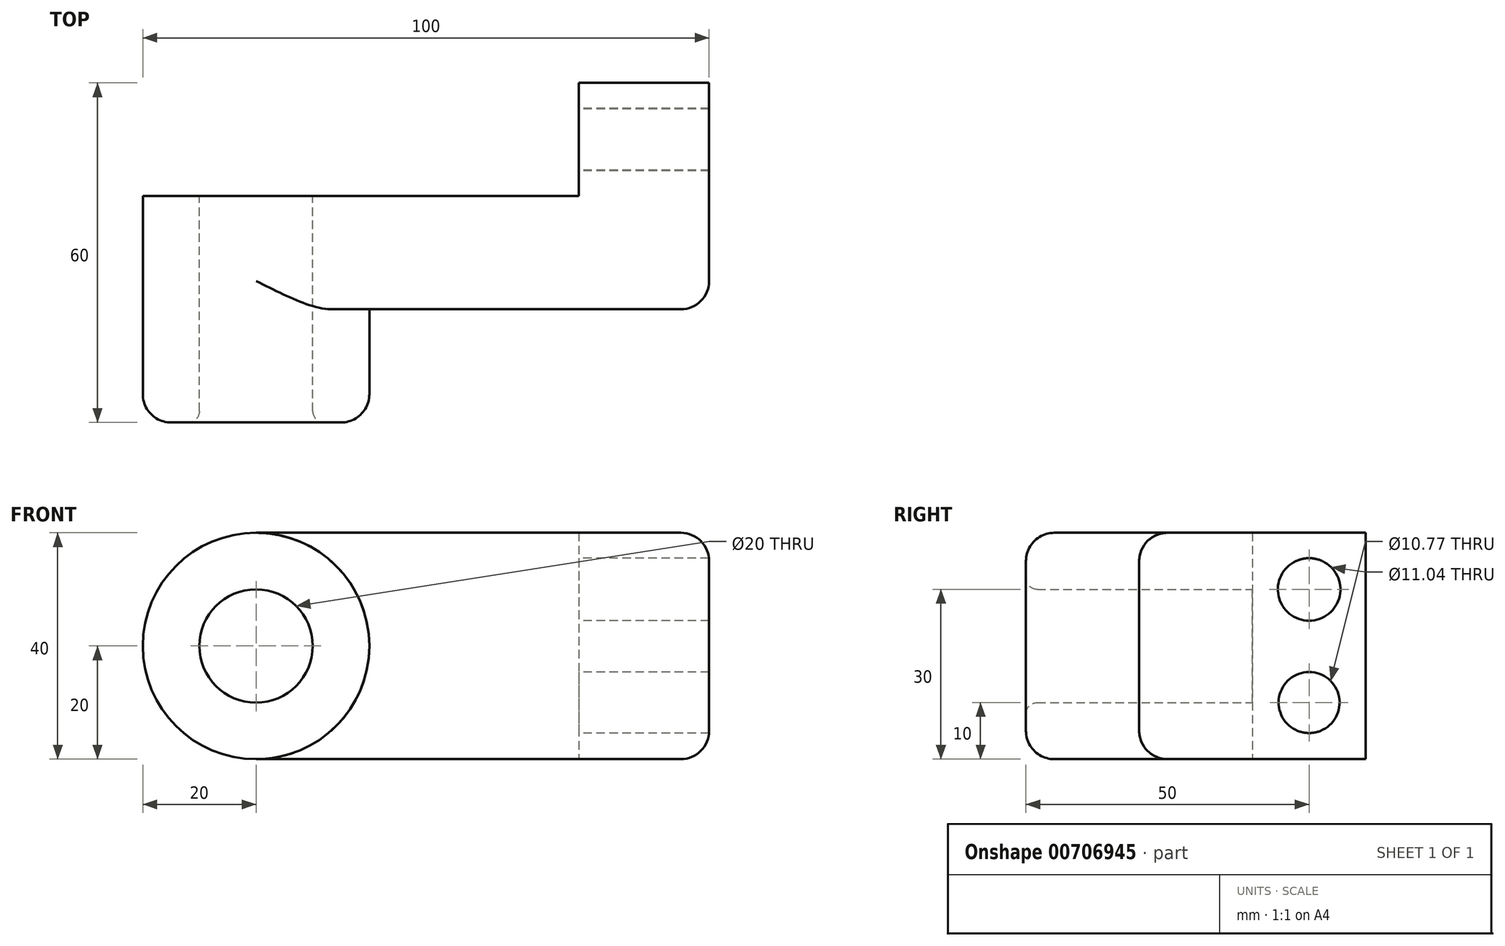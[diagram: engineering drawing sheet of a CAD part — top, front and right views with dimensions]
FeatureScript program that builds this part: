
annotation { "Feature Type Name" : "Feature", "Feature Type Description" : "" }
export const myFeature = defineFeature(function(context is Context, id is Id, definition is map)
    precondition{}
    {
        {
            var Q0;
            Q0=qCreatedBy(makeId("Front.planeOp"),FACE);
            var sketch = newSketch(context, id + "F0", { "sketchPlane" : qUnion([Q0])});
            skCircle(sketch, "E0", {"center": v(0, 0) * mm, "radius": 10 * mm});
            skCircle(sketch, "E1", {"center": v(0, 0) * mm, "radius": 20 * mm});
            skLineSegment(sketch, "E2", {"start": v(0, 20) * mm, "end": v(80, 20) * mm});
            skLineSegment(sketch, "E3", {"start": v(0, -20) * mm, "end": v(80, -20) * mm});
            skLineSegment(sketch, "E4", {"start": v(80, 20) * mm, "end": v(80, -20) * mm});
            skLineSegment(sketch, "E5", {"start": v(56.97, 20) * mm, "end": v(56.97, -20) * mm});
            skSolve(sketch);
        }
        {
            var Q0;
            Q0=makeQuery(id+"F0.imprint","IMPRINT",FACE,{"disambiguationData":[TD([[makeQuery(id+"F0.imprint","IMPRINT",EDGE,{"derivedFrom":sQuery(id+"F0.wireOp",EDGE,"E0")}),-1.0]])]});
            extrude(context, id + "F1", {"entities" : qUnion([Q0]), "surfaceOperationType" : NewSurfaceOperationType.ADD, "depth" : 40 * mm, "offsetDistance" : 25 * mm});
        }
        {
            var Q0;
            {var subQ0=sQuery(id+"F0.wireOp",EDGE,"E2");Q0=makeQuery(id+"F0.imprint","IMPRINT",FACE,{"disambiguationData":[TD([[makeQuery(id+"F0.imprint","IMPRINT",EDGE,{"derivedFrom":subQ0}),-1.0]])]});}
            extrude(context, id + "F2", {"entities" : qUnion([Q0]), "operationType" : NewBodyOperationType.ADD, "depth" : 20 * mm, "offsetDistance" : 25 * mm});
        }
        {
            var Q0;
            {var subQ0=sQuery(id+"F0.wireOp",EDGE,"E4");Q0=makeQuery(id+"F0.imprint","IMPRINT",FACE,{"disambiguationData":[TD([[makeQuery(id+"F0.imprint","IMPRINT",EDGE,{"derivedFrom":subQ0}),-1.0]])]});}
            extrude(context, id + "F3", {"entities" : qUnion([Q0]), "operationType" : NewBodyOperationType.ADD, "oppositeDirection" : true, "depth" : 20 * mm, "offsetDistance" : 25 * mm});
        }
        {
            var Q0;
            Q0=makeQuery(id+"F3.opExtrude","SWEPT_FACE",FACE,{"disambiguationData":[OSD([sQuery(id+"F0.wireOp",EDGE,"E5")])]});
            var sketch = newSketch(context, id + "F4", { "sketchPlane" : qUnion([Q0])});
            skCircle(sketch, "E6", {"center": v(-10, 10) * mm, "radius": 5.52 * mm});
            skPoint(sketch, "E6.centerSnap0", {"position": v(-10, 20) * mm});
            skCircle(sketch, "E7", {"center": v(-10, -10) * mm, "radius": 5.39 * mm});
            skPoint(sketch, "E7.centerSnap0", {"position": v(-10, -20) * mm});
            skSolve(sketch);
        }
        {
            var Q0;
            Q0 = qSketchRegion(id + "F4", true);
            extrude(context, id + "F5", {"entities" : qUnion([Q0]), "operationType" : NewBodyOperationType.REMOVE, "oppositeDirection" : true, "depth" : 28.9 * mm, "offsetDistance" : 25 * mm});
        }
        {
            var Q0;
            Q0=makeQuery(id+"F1.opExtrude","CAP_EDGE",EDGE,{"disambiguationData":[OSD([sQuery(id+"F0.wireOp",EDGE,"E0")])],"isStart":false});
            fillet(context, id + "F6", {"entities" : qUnion([Q0]), "radius" : 2 * mm, "tangentPropagation" : true, "allowEdgeOverflow" : false});
        }
        {
            var Q0;
            {var subQ0=sQuery(id+"F0.wireOp",EDGE,"E3");Q0=makeQuery(id+"F6.opFillet","BLEND_EDGE",EDGE,{"blendedFrom":[makeQuery(id+"F2.opExtrude","CAP_EDGE",EDGE,{"disambiguationData":[OSD([subQ0])],"isStart":false}),makeQuery(id+"F2.opExtrude","CAP_FACE",FACE,{"disambiguationData":[OSD([sQuery(id+"F0.wireOp",EDGE,"E1"),sQuery(id+"F0.wireOp",EDGE,"E2"),subQ0,sQuery(id+"F0.wireOp",EDGE,"E4")])],"isStart":false})],"blendedInto":[makeQuery(id+"F2.opExtrude","CAP_FACE",FACE,{"disambiguationData":[OSD([sQuery(id+"F0.wireOp",EDGE,"E1"),sQuery(id+"F0.wireOp",EDGE,"E2"),subQ0,sQuery(id+"F0.wireOp",EDGE,"E4")])],"isStart":false})]});}
            var Q1;
            Q1=makeQuery(id+"F2.opExtrude","CAP_EDGE",EDGE,{"disambiguationData":[OSD([sQuery(id+"F0.wireOp",EDGE,"E2")])],"isStart":false});
            var Q2;
            Q2=makeQuery(id+"F2.opExtrude","CAP_EDGE",EDGE,{"disambiguationData":[OSD([sQuery(id+"F0.wireOp",EDGE,"E3")])],"isStart":false});
            var Q3;
            Q3=makeQuery(id+"F2.opExtrude","CAP_EDGE",EDGE,{"disambiguationData":[OSD([sQuery(id+"F0.wireOp",EDGE,"E1")])],"isStart":false});
            fillet(context, id + "F7", {"entities" : qUnion([Q0, Q1, Q2, Q3]), "radius" : 5 * mm, "tangentPropagation" : true, "allowEdgeOverflow" : false});
        }
        {
            var Q0;
            {var subQ0=sQuery(id+"F0.wireOp",EDGE,"E4");var subQ1=sQuery(id+"F0.wireOp",EDGE,"E3");Q0=makeQuery(id+"F3.boolean.opBoolean","MERGE",EDGE,{"derivedFrom":[makeQuery(id+"F2.opExtrude","SWEPT_EDGE",EDGE,{"disambiguationData":[OSD([subQ1,subQ0])]}),makeQuery(id+"F3.opExtrude","SWEPT_EDGE",EDGE,{"disambiguationData":[OSD([subQ1,subQ0])]})]});}
            var Q1;
            {var subQ0=sQuery(id+"F0.wireOp",EDGE,"E4");var subQ1=sQuery(id+"F0.wireOp",EDGE,"E2");Q1=makeQuery(id+"F3.boolean.opBoolean","MERGE",EDGE,{"derivedFrom":[makeQuery(id+"F2.opExtrude","SWEPT_EDGE",EDGE,{"disambiguationData":[OSD([subQ1,subQ0])]}),makeQuery(id+"F3.opExtrude","SWEPT_EDGE",EDGE,{"disambiguationData":[OSD([subQ1,subQ0])]})]});}
            fillet(context, id + "F8", {"entities" : qUnion([Q0, Q1]), "radius" : 5 * mm, "tangentPropagation" : true, "allowEdgeOverflow" : false});
        }
        {
            var Q0;
            Q0=makeQuery(id+"F1.opExtrude","CAP_EDGE",EDGE,{"disambiguationData":[OSD([sQuery(id+"F0.wireOp",EDGE,"E1")])],"isStart":false});
            fillet(context, id + "F9", {"entities" : qUnion([Q0]), "radius" : 5 * mm, "tangentPropagation" : true, "allowEdgeOverflow" : false});
        }
    });
